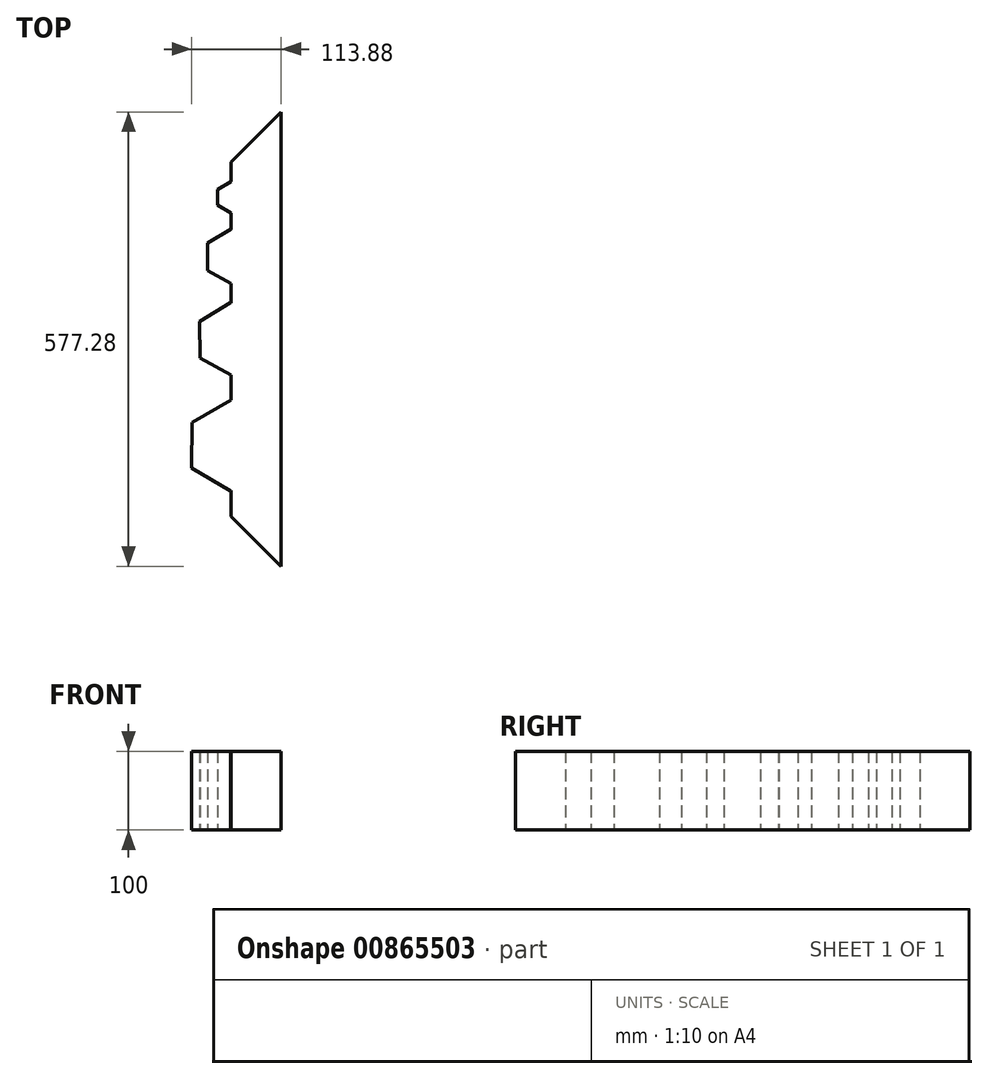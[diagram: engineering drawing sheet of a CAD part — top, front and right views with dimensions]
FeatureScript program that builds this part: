
annotation { "Feature Type Name" : "Feature", "Feature Type Description" : "" }
export const myFeature = defineFeature(function(context is Context, id is Id, definition is map)
    precondition{}
    {
        {
            var Q0;
            Q0=qCreatedBy(makeId("Top.planeOp"),FACE);
            var sketch = newSketch(context, id + "F0", { "sketchPlane" : qUnion([Q0])});
            skLineSegment(sketch, "E0.bottom", {"start": v(0, 0) * mm, "end": v(450, 0) * mm});
            skLineSegment(sketch, "E0.top", {"start": v(0, -450) * mm, "end": v(450, -450) * mm});
            skLineSegment(sketch, "E0.left", {"start": v(0, 0) * mm, "end": v(0, -450) * mm});
            skLineSegment(sketch, "E0.right", {"start": v(450, 0) * mm, "end": v(450, -450) * mm});
            skCircle(sketch, "E1", {"center": v(32.5, 0) * mm, "radius": 7.5 * mm});
            skCircle(sketch, "E2", {"center": v(70, 0) * mm, "radius": 10 * mm});
            skCircle(sketch, "E3", {"center": v(112.5, 0) * mm, "radius": 12.5 * mm});
            skCircle(sketch, "E4", {"center": v(212.5, 0) * mm, "radius": 17.5 * mm});
            skCircle(sketch, "E5", {"center": v(270, 0) * mm, "radius": 20 * mm});
            skPoint(sketch, "E6", {"position": v(0, -225) * mm});
            skCircle(sketch, "E7", {"center": v(160, 0) * mm, "radius": 15 * mm});
            skCircle(sketch, "E8", {"center": v(332.5, 0) * mm, "radius": 22.5 * mm});
            skCircle(sketch, "E9", {"center": v(400, 0) * mm, "radius": 25 * mm});
            skCircle(sketch, "E10", {"center": v(0, -50) * mm, "radius": 27.5 * mm});
            skCircle(sketch, "E11", {"center": v(0, -127.5) * mm, "radius": 30 * mm});
            skCircle(sketch, "E12", {"center": v(0, -210) * mm, "radius": 32.5 * mm});
            skCircle(sketch, "E13", {"center": v(0, -297.5) * mm, "radius": 35 * mm});
            skCircle(sketch, "E14", {"center": v(0, -390) * mm, "radius": 37.5 * mm});
            skCircle(sketch, "E15.cCircle", {"center": v(450, -45) * mm, "radius": 20 * mm, "construction": true});
            skLineSegment(sketch, "E15.0", {"start": v(450, -65) * mm, "end": v(432.68, -55) * mm});
            skLineSegment(sketch, "E15.1", {"start": v(432.68, -55) * mm, "end": v(432.68, -35) * mm});
            skLineSegment(sketch, "E15.2", {"start": v(432.68, -35) * mm, "end": v(450, -25) * mm});
            skLineSegment(sketch, "E15.3", {"start": v(450, -25) * mm, "end": v(467.32, -35) * mm});
            skLineSegment(sketch, "E15.4", {"start": v(467.32, -35) * mm, "end": v(467.32, -55) * mm});
            skLineSegment(sketch, "E15.5", {"start": v(467.32, -55) * mm, "end": v(450, -65) * mm});
            skCircle(sketch, "E16.cCircle", {"center": v(450, -120) * mm, "radius": 34.64 * mm, "construction": true});
            skLineSegment(sketch, "E16.0", {"start": v(420.17, -137.61) * mm, "end": v(419.83, -102.97) * mm});
            skLineSegment(sketch, "E16.1", {"start": v(419.83, -102.97) * mm, "end": v(449.66, -85.36) * mm});
            skLineSegment(sketch, "E16.2", {"start": v(449.66, -85.36) * mm, "end": v(479.83, -102.39) * mm});
            skLineSegment(sketch, "E16.3", {"start": v(479.83, -102.39) * mm, "end": v(480.17, -137.03) * mm});
            skLineSegment(sketch, "E16.4", {"start": v(480.17, -137.03) * mm, "end": v(450.34, -154.64) * mm});
            skLineSegment(sketch, "E16.5", {"start": v(450.34, -154.64) * mm, "end": v(420.17, -137.61) * mm});
            skCircle(sketch, "E17.cCircle", {"center": v(450, -225) * mm, "radius": 46.19 * mm, "construction": true});
            skLineSegment(sketch, "E17.0", {"start": v(410.35, -248.7) * mm, "end": v(409.66, -202.51) * mm});
            skLineSegment(sketch, "E17.1", {"start": v(409.66, -202.51) * mm, "end": v(449.3, -178.82) * mm});
            skLineSegment(sketch, "E17.2", {"start": v(449.3, -178.82) * mm, "end": v(489.65, -201.3) * mm});
            skLineSegment(sketch, "E17.3", {"start": v(489.65, -201.3) * mm, "end": v(490.34, -247.49) * mm});
            skLineSegment(sketch, "E17.4", {"start": v(490.34, -247.49) * mm, "end": v(450.7, -271.18) * mm});
            skLineSegment(sketch, "E17.5", {"start": v(450.7, -271.18) * mm, "end": v(410.35, -248.7) * mm});
            skCircle(sketch, "E18.cCircle", {"center": v(450, -360) * mm, "radius": 57.74 * mm, "construction": true});
            skLineSegment(sketch, "E18.0", {"start": v(400.24, -330.72) * mm, "end": v(450.48, -302.27) * mm});
            skLineSegment(sketch, "E18.1", {"start": v(450.48, -302.27) * mm, "end": v(500.24, -331.55) * mm});
            skLineSegment(sketch, "E18.2", {"start": v(500.24, -331.55) * mm, "end": v(499.76, -389.28) * mm});
            skLineSegment(sketch, "E18.3", {"start": v(499.76, -389.28) * mm, "end": v(449.52, -417.73) * mm});
            skLineSegment(sketch, "E18.4", {"start": v(449.52, -417.73) * mm, "end": v(399.76, -388.45) * mm});
            skLineSegment(sketch, "E18.5", {"start": v(399.76, -388.45) * mm, "end": v(400.24, -330.72) * mm});
            skLineSegment(sketch, "E19", {"start": v(420, -450) * mm, "end": v(412.5, -437) * mm});
            skLineSegment(sketch, "E20", {"start": v(412.5, -437) * mm, "end": v(405, -450) * mm});
            skLineSegment(sketch, "E21", {"start": v(420, -450) * mm, "end": v(405, -450) * mm});
            skLineSegment(sketch, "E22", {"start": v(375, -450) * mm, "end": v(362.5, -428.35) * mm});
            skLineSegment(sketch, "E23", {"start": v(362.5, -428.35) * mm, "end": v(350, -450) * mm});
            skLineSegment(sketch, "E24", {"start": v(350, -450) * mm, "end": v(375, -450) * mm});
            skLineSegment(sketch, "E25", {"start": v(320, -450) * mm, "end": v(305, -424.02) * mm});
            skLineSegment(sketch, "E26", {"start": v(305, -424.02) * mm, "end": v(290, -450) * mm});
            skLineSegment(sketch, "E27", {"start": v(290, -450) * mm, "end": v(320, -450) * mm});
            skLineSegment(sketch, "E28", {"start": v(260, -450) * mm, "end": v(220, -450) * mm});
            skLineSegment(sketch, "E29", {"start": v(220, -450) * mm, "end": v(240, -415.36) * mm});
            skLineSegment(sketch, "E30", {"start": v(240, -415.36) * mm, "end": v(260, -450) * mm});
            skLineSegment(sketch, "E31", {"start": v(190, -450) * mm, "end": v(140, -450) * mm});
            skLineSegment(sketch, "E32", {"start": v(140, -450) * mm, "end": v(165, -406.7) * mm});
            skLineSegment(sketch, "E33", {"start": v(165, -406.7) * mm, "end": v(190, -450) * mm});
            skLineSegment(sketch, "E34", {"start": v(110, -450) * mm, "end": v(50, -450) * mm});
            skLineSegment(sketch, "E35", {"start": v(50, -450) * mm, "end": v(80, -398.04) * mm});
            skLineSegment(sketch, "E36", {"start": v(80, -398.04) * mm, "end": v(110, -450) * mm});
            skCircle(sketch, "E37", {"center": v(366.86, -63.19) * mm, "radius": 8.5 * mm});
            skCircle(sketch, "E38", {"center": v(306.86, -63.19) * mm, "radius": 11.5 * mm});
            skCircle(sketch, "E39", {"center": v(237.86, -63.19) * mm, "radius": 17.5 * mm});
            skCircle(sketch, "E40", {"center": v(172.86, -63.19) * mm, "radius": 22.5 * mm});
            skCircle(sketch, "E41", {"center": v(90.36, -63.19) * mm, "radius": 30 * mm});
            skPoint(sketch, "E42.cornerSnap0", {"position": v(400, -359.59) * mm});
            skEllipse(sketch, "E43", {"center": v(355, -158.3) * mm, "majorRadius": 69.57 * mm, "minorRadius": 24.91 * mm, "majorAxis": v(0, -1)});
            skEllipse(sketch, "E44", {"center": v(255, -158.3) * mm, "majorRadius": 57.98 * mm, "minorRadius": 25.3 * mm, "majorAxis": v(0, -1)});
            skEllipse(sketch, "E45", {"center": v(160, -158.3) * mm, "majorRadius": 47.06 * mm, "minorRadius": 19.98 * mm, "majorAxis": v(0, -1)});
            skEllipse(sketch, "E46", {"center": v(75, -158.3) * mm, "majorRadius": 42.97 * mm, "minorRadius": 16.37 * mm, "majorAxis": v(0, -1)});
            skLineSegment(sketch, "E47.bottom", {"start": v(132.9, -316.06) * mm, "end": v(52.9, -316.06) * mm});
            skLineSegment(sketch, "E47.top", {"start": v(132.9, -236.06) * mm, "end": v(52.9, -236.06) * mm});
            skLineSegment(sketch, "E47.left", {"start": v(132.9, -316.06) * mm, "end": v(132.9, -236.06) * mm});
            skLineSegment(sketch, "E47.right", {"start": v(52.9, -316.06) * mm, "end": v(52.9, -236.06) * mm});
            skPoint(sketch, "E47.middle", {"position": v(92.9, -276.06) * mm});
            skLineSegment(sketch, "E48.bottom", {"start": v(232.94, -306.06) * mm, "end": v(172.94, -306.06) * mm});
            skLineSegment(sketch, "E48.top", {"start": v(232.94, -246.06) * mm, "end": v(172.94, -246.06) * mm});
            skLineSegment(sketch, "E48.left", {"start": v(232.94, -306.06) * mm, "end": v(232.94, -246.06) * mm});
            skLineSegment(sketch, "E48.right", {"start": v(172.94, -306.06) * mm, "end": v(172.94, -246.06) * mm});
            skPoint(sketch, "E48.middle", {"position": v(202.94, -276.06) * mm});
            skLineSegment(sketch, "E49.bottom", {"start": v(312.28, -296.06) * mm, "end": v(272.28, -296.06) * mm});
            skLineSegment(sketch, "E49.top", {"start": v(312.28, -256.06) * mm, "end": v(272.28, -256.06) * mm});
            skLineSegment(sketch, "E49.left", {"start": v(312.28, -296.06) * mm, "end": v(312.28, -256.06) * mm});
            skLineSegment(sketch, "E49.right", {"start": v(272.28, -296.06) * mm, "end": v(272.28, -256.06) * mm});
            skPoint(sketch, "E49.middle", {"position": v(292.28, -276.06) * mm});
            skLineSegment(sketch, "E50.bottom", {"start": v(372.3, -286.06) * mm, "end": v(352.3, -286.06) * mm});
            skLineSegment(sketch, "E50.top", {"start": v(372.3, -266.06) * mm, "end": v(352.3, -266.06) * mm});
            skLineSegment(sketch, "E50.left", {"start": v(372.3, -286.06) * mm, "end": v(372.3, -266.06) * mm});
            skLineSegment(sketch, "E50.right", {"start": v(352.3, -286.06) * mm, "end": v(352.3, -266.06) * mm});
            skPoint(sketch, "E50.middle", {"position": v(362.3, -276.06) * mm});
            skLineSegment(sketch, "E51.bottom", {"start": v(80, -382.47) * mm, "end": v(60, -382.47) * mm});
            skLineSegment(sketch, "E51.top", {"start": v(80, -372.47) * mm, "end": v(60, -372.47) * mm});
            skLineSegment(sketch, "E51.left", {"start": v(80, -382.47) * mm, "end": v(80, -372.47) * mm});
            skLineSegment(sketch, "E51.right", {"start": v(60, -382.47) * mm, "end": v(60, -372.47) * mm});
            skPoint(sketch, "E51.middle", {"position": v(70, -377.47) * mm});
            skLineSegment(sketch, "E52.bottom", {"start": v(110, -387.47) * mm, "end": v(150, -387.47) * mm});
            skLineSegment(sketch, "E52.top", {"start": v(110, -367.47) * mm, "end": v(150, -367.47) * mm});
            skLineSegment(sketch, "E52.left", {"start": v(110, -387.47) * mm, "end": v(110, -367.47) * mm});
            skLineSegment(sketch, "E52.right", {"start": v(150, -387.47) * mm, "end": v(150, -367.47) * mm});
            skPoint(sketch, "E52.middle", {"position": v(130, -377.47) * mm});
            skLineSegment(sketch, "E53.bottom", {"start": v(190, -392.47) * mm, "end": v(250, -392.47) * mm});
            skLineSegment(sketch, "E53.top", {"start": v(190, -362.47) * mm, "end": v(250, -362.47) * mm});
            skLineSegment(sketch, "E53.left", {"start": v(190, -392.47) * mm, "end": v(190, -362.47) * mm});
            skLineSegment(sketch, "E53.right", {"start": v(250, -392.47) * mm, "end": v(250, -362.47) * mm});
            skPoint(sketch, "E53.middle", {"position": v(220, -377.47) * mm});
            skLineSegment(sketch, "E54.bottom", {"start": v(375, -397.47) * mm, "end": v(295, -397.47) * mm});
            skLineSegment(sketch, "E54.top", {"start": v(375, -357.47) * mm, "end": v(295, -357.47) * mm});
            skLineSegment(sketch, "E54.left", {"start": v(375, -397.47) * mm, "end": v(375, -357.47) * mm});
            skLineSegment(sketch, "E54.right", {"start": v(295, -397.47) * mm, "end": v(295, -357.47) * mm});
            skPoint(sketch, "E54.middle", {"position": v(335, -377.47) * mm});
            skLineSegment(sketch, "E55", {"start": v(0, 0) * mm, "end": v(-63.64, 63.64) * mm});
            skLineSegment(sketch, "E56", {"start": v(-63.64, 63.64) * mm, "end": v(513.64, 63.64) * mm});
            skLineSegment(sketch, "E57", {"start": v(513.64, 63.64) * mm, "end": v(450, 0) * mm});
            skLineSegment(sketch, "E58", {"start": v(513.64, 63.64) * mm, "end": v(513.64, -513.64) * mm});
            skLineSegment(sketch, "E59", {"start": v(513.64, -513.64) * mm, "end": v(450, -450) * mm});
            skLineSegment(sketch, "E60", {"start": v(-63.64, 63.64) * mm, "end": v(-63.64, -513.64) * mm});
            skLineSegment(sketch, "E61", {"start": v(-63.64, -513.64) * mm, "end": v(0, -450) * mm});
            skLineSegment(sketch, "E62", {"start": v(-63.64, -513.64) * mm, "end": v(513.64, -513.64) * mm});
            skSolve(sketch);
        }
        {
            var Q0;
            {var subQ16=sQuery(id+"F0.wireOp",EDGE,"E15.3");Q0=makeQuery(id+"F0.imprint","IMPRINT",FACE,{"disambiguationData":[TD([[makeQuery(id+"F0.imprint","IMPRINT",EDGE,{"derivedFrom":subQ16}),1.0]])]});}
            var Q1;
            {var subQ2=sQuery(id+"F0.wireOp",EDGE,"E15.3");Q1=makeQuery(id+"F0.imprint","IMPRINT",FACE,{"disambiguationData":[TD([[makeQuery(id+"F0.imprint","IMPRINT",EDGE,{"derivedFrom":subQ2}),-1.0]])]});}
            var Q2;
            {var subQ0=sQuery(id+"F0.wireOp",EDGE,"E15.0");Q2=makeQuery(id+"F0.imprint","IMPRINT",FACE,{"disambiguationData":[TD([[makeQuery(id+"F0.imprint","IMPRINT",EDGE,{"derivedFrom":subQ0}),-1.0]])]});}
            var Q3;
            {var subQ1=sQuery(id+"F0.wireOp",EDGE,"E16.0");Q3=makeQuery(id+"F0.imprint","IMPRINT",FACE,{"disambiguationData":[TD([[makeQuery(id+"F0.imprint","IMPRINT",EDGE,{"derivedFrom":subQ1}),-1.0]])]});}
            var Q4;
            {var subQ1=sQuery(id+"F0.wireOp",EDGE,"E16.3");Q4=makeQuery(id+"F0.imprint","IMPRINT",FACE,{"disambiguationData":[TD([[makeQuery(id+"F0.imprint","IMPRINT",EDGE,{"derivedFrom":subQ1}),-1.0]])]});}
            var Q5;
            {var subQ1=sQuery(id+"F0.wireOp",EDGE,"E17.3");Q5=makeQuery(id+"F0.imprint","IMPRINT",FACE,{"disambiguationData":[TD([[makeQuery(id+"F0.imprint","IMPRINT",EDGE,{"derivedFrom":subQ1}),-1.0]])]});}
            var Q6;
            {var subQ4=sQuery(id+"F0.wireOp",EDGE,"E17.0");Q6=makeQuery(id+"F0.imprint","IMPRINT",FACE,{"disambiguationData":[TD([[makeQuery(id+"F0.imprint","IMPRINT",EDGE,{"derivedFrom":subQ4}),-1.0]])]});}
            var Q7;
            {var subQ0=sQuery(id+"F0.wireOp",EDGE,"E18.4");Q7=makeQuery(id+"F0.imprint","IMPRINT",FACE,{"disambiguationData":[TD([[makeQuery(id+"F0.imprint","IMPRINT",EDGE,{"derivedFrom":subQ0}),-1.0]])]});}
            var Q8;
            {var subQ1=sQuery(id+"F0.wireOp",EDGE,"E18.1");Q8=makeQuery(id+"F0.imprint","IMPRINT",FACE,{"disambiguationData":[TD([[makeQuery(id+"F0.imprint","IMPRINT",EDGE,{"derivedFrom":subQ1}),-1.0]])]});}
            extrude(context, id + "F1", {"entities" : qUnion([Q0, Q1, Q2, Q3, Q4, Q5, Q6, Q7, Q8]), "depth" : 100 * mm, "offsetDistance" : 25 * mm});
        }
    });
